# Revit family: Storage-Freestanding-Teknion-BSUOS_Storage_Unit_Open_Shelves-R2019
name_source: partatom
category: Furniture
units: mm (PartAtom-declared; Revit-internal decimal feet)

## family parameters
Always vertical = Yes
Cut with Voids When Loaded = No
OmniClass Number = 23.40.20.00
OmniClass Title = General Furniture and Specialties
Room Calculation Point = No
Shared = Yes
Work Plane-Based = No

## types (3) — shared parameters
Assembly Code = E2020200
Manufacturer = Teknion
Manufacturer Fax = 416.661.4586
Part Number = BSUOS
Product Documentation Link = https://www.teknion.com
Product Line = Expansion Casegoods
Product Page URL = https://www.teknion.com
Series = Expansion Casegoods
Sustainability Data = https://www.teknion.com
URL = www.teknion.com
Unit Weight URL = http://www.teknion.com
Warranty = http://www.teknion.com

## per-type parameters (varying)
| type | Depth | Description | Model |
| 24" Depth, Pull Storage Style | 24 " | Storage Unit - Open Shelves, Pulls, 24" Depth | BSUOSP24____ |
| 20" Depth, Pull Storage Style | 20 " | Storage Unit - Open Shelves, Pulls, 20" Depth | BSUOSP20____ |
| 18" Depth, Pull Storage Style | 18 " | Storage Unit - Open Shelves, Pulls, 18" Depth | BSUOSP18____ |

## geometry (parser evidence)
native form markers: Sweep x2
no freeform markers — native parametric forms only
